# Revit family: Furniture_Chairs-Stools-Benches_KUMI_Sittbank
name_source: partatom
category: Furniture
revit_build: Autodesk Revit 2018 (Build: 20190510_1515(x64)
units: mm (PartAtom-declared; Revit-internal decimal feet)

## family parameters
Always vertical = No
Cut with Voids When Loaded = No
OmniClass Number = 23.21.23.13.19
OmniClass Title = Residential Benches
Room Calculation Point = No
Shared = No
Work Plane-Based = Yes

## types (1)
- Furniture_Chairs-Stools-Benches_KUMI_Sittbank
    BIMobject category = Chairs, Stools & Benches
    Cover Material = Kumi - Plastic - Black
    Default Elevation = 0 mm  [stored 0 ft]
    Description = Bench (double section) in black laminate with backboard and hook strip. A stable, double-sided and free-standing bench for, for example, the dressing room. The bench has a seat height of 430 mm and the seat depth is 365 mm. Total height 1600 mm. Powder-coated base in black RAL 9005.
    Design country = Sweden
    Edition number = 1
    Frame Material = Kumi - Steel - Black
    Manufacturer = KUMI
    Manufacturer country = Sweden
    Manufacturer name = KUMI
    Model = Bench Double section - 1000 mm - 2-655
    Product Guid = 01cd42ce-a9ab-4656-8ae6-959b6a40a55d
    Product SKU = kumi-sittbank-bench
    Product data url = https://bimobject.com
    Product name = Sittbänk
    Product url = https://www.kumi.se
    QR code = https://bimobject.com
    Type - (Bench Double section 1000 mm) = Yes
    Type - (Bench Double section 1500 mm) = No
    Type - (Bench Double section 2000 mm) = No
    Type - (Bench Single section 1000 mm) = No
    Type - (Bench Single section 1500 mm) = No
    Type - (Bench Single section 2000 mm) = No
    URL = https://www.kumi.se

note: [stored X ft] marks values corroborated as IEEE doubles in the binary element streams (Revit-internal decimal feet)

## geometry (parser evidence)
native form markers: Sweep x3
no freeform markers — native parametric forms only
